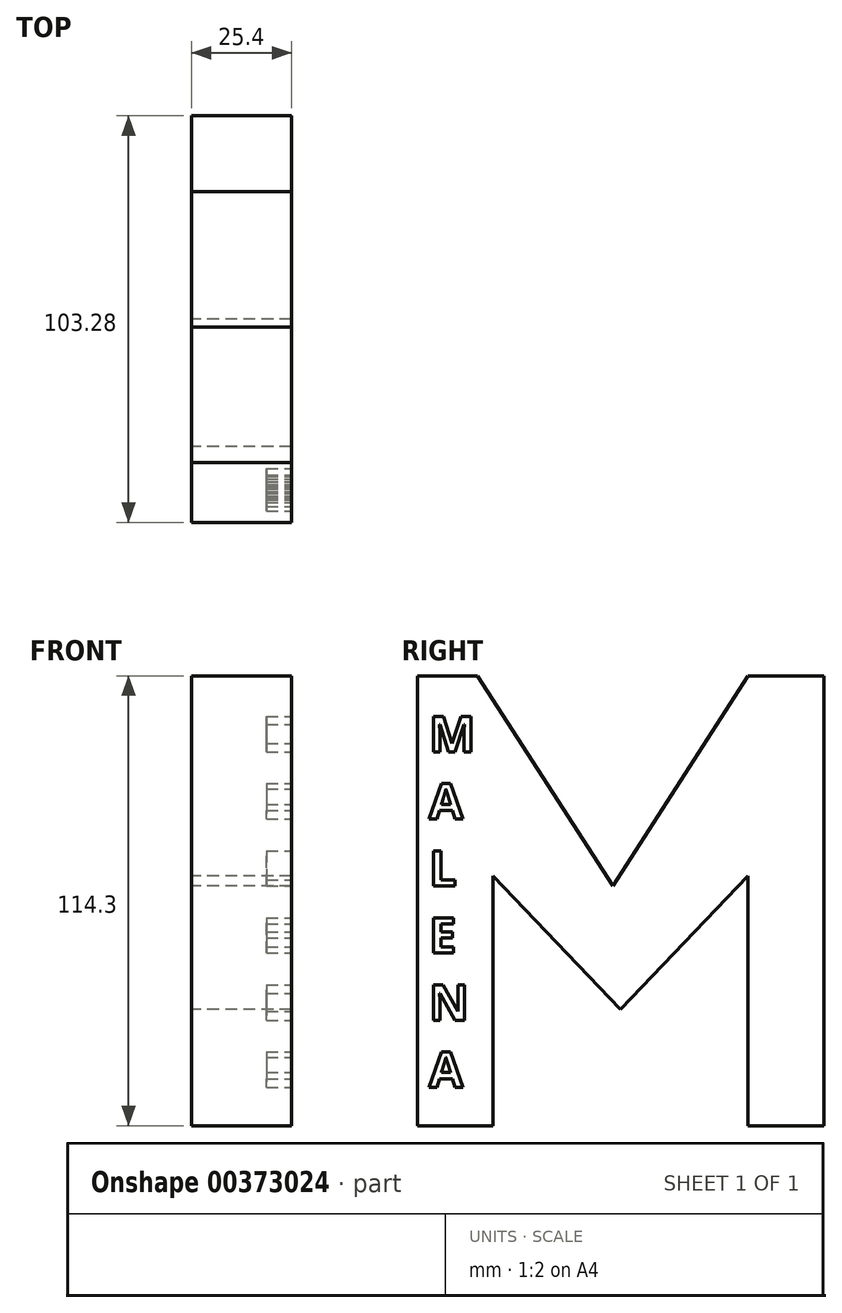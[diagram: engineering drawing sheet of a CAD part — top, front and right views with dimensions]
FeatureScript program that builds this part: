
annotation { "Feature Type Name" : "Feature", "Feature Type Description" : "" }
export const myFeature = defineFeature(function(context is Context, id is Id, definition is map)
    precondition{}
    {
        {
            var Q0;
            Q0=qCreatedBy(makeId("Right.planeOp"),FACE);
            var sketch = newSketch(context, id + "F0", { "sketchPlane" : qUnion([Q0])});
            skLineSegment(sketch, "E0", {"start": v(-62.9, 50.8) * mm, "end": v(-43.65, 50.8) * mm});
            skLineSegment(sketch, "E1", {"start": v(-43.65, 50.8) * mm, "end": v(-9.26, -2.58) * mm});
            skLineSegment(sketch, "E2", {"start": v(-9.26, -2.58) * mm, "end": v(25.14, 50.8) * mm});
            skLineSegment(sketch, "E3", {"start": v(25.14, 50.8) * mm, "end": v(44.4, 50.8) * mm});
            skLineSegment(sketch, "E4", {"start": v(44.4, 50.8) * mm, "end": v(44.4, -63.5) * mm});
            skLineSegment(sketch, "E5", {"start": v(44.4, -63.5) * mm, "end": v(25.14, -63.5) * mm});
            skLineSegment(sketch, "E6", {"start": v(25.14, -63.5) * mm, "end": v(25.14, 0) * mm});
            skLineSegment(sketch, "E7", {"start": v(25.14, 0) * mm, "end": v(-7.3, -33.99) * mm});
            skLineSegment(sketch, "E8", {"start": v(-7.3, -33.99) * mm, "end": v(-39.62, 0) * mm});
            skLineSegment(sketch, "E9", {"start": v(-39.62, 0) * mm, "end": v(-39.62, -63.5) * mm});
            skLineSegment(sketch, "E10", {"start": v(-39.62, -63.5) * mm, "end": v(-58.88, -63.5) * mm});
            skLineSegment(sketch, "E11", {"start": v(-58.88, -63.5) * mm, "end": v(-58.88, 50.8) * mm});
            skSolve(sketch);
        }
        {
            var Q0;
            Q0 = qSketchRegion(id + "F0", true);
            extrude(context, id + "F1", {"entities" : qUnion([Q0]), "depth" : 25.4 * mm});
        }
        {
            var Q0;
            Q0=makeQuery(id+"F1.opExtrude","CAP_FACE",FACE,{"disambiguationData":[OSD([sQuery(id+"F0.wireOp",EDGE,"E0"),sQuery(id+"F0.wireOp",EDGE,"E1"),sQuery(id+"F0.wireOp",EDGE,"E2"),sQuery(id+"F0.wireOp",EDGE,"E3"),sQuery(id+"F0.wireOp",EDGE,"E4"),sQuery(id+"F0.wireOp",EDGE,"E5"),sQuery(id+"F0.wireOp",EDGE,"E6"),sQuery(id+"F0.wireOp",EDGE,"E7"),sQuery(id+"F0.wireOp",EDGE,"E8"),sQuery(id+"F0.wireOp",EDGE,"E9"),sQuery(id+"F0.wireOp",EDGE,"E10"),sQuery(id+"F0.wireOp",EDGE,"E11")])],"isStart":false});
            var sketch = newSketch(context, id + "F2", { "sketchPlane" : qUnion([Q0])});
            skText(sketch, "E12", { "text": "M\nA\nL\nE\nN\nA", "fontName": "OpenSans-Bold.ttf"});
            skPoint(sketch, "E13", {"position": v(-51.27, 50.8) * mm});
            const initialGuessF2  = {"E12": [-0.05596, 0.03146, 1, 0, 0.00902]};
            skSetInitialGuess(sketch, initialGuessF2);
            skSolve(sketch);
        }
        {
            var Q0;
            Q0 = qSketchRegion(id + "F2", true);
            extrude(context, id + "F3", {"entities" : qUnion([Q0]), "operationType" : NewBodyOperationType.REMOVE, "oppositeDirection" : true, "depth" : 6.35 * mm});
        }
    });
